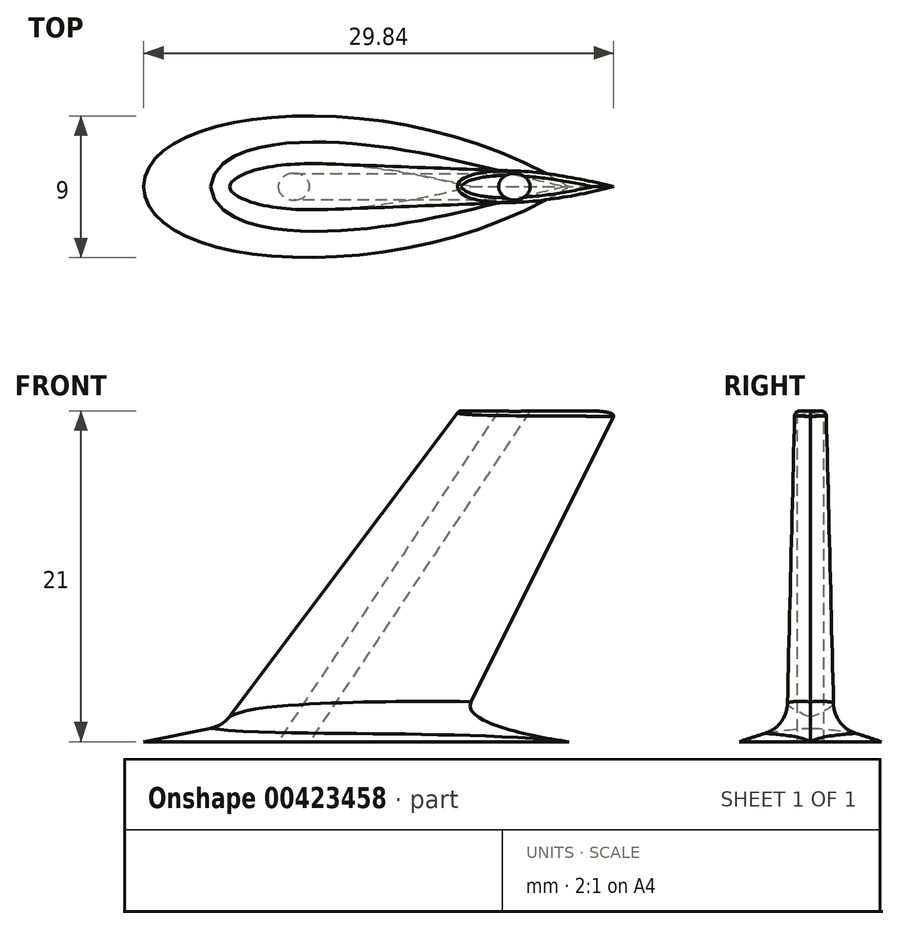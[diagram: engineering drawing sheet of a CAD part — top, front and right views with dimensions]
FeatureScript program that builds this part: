
annotation { "Feature Type Name" : "Feature", "Feature Type Description" : "" }
export const myFeature = defineFeature(function(context is Context, id is Id, definition is map)
    precondition{}
    {
        {
            var Q0;
            Q0=qCreatedBy(makeId("Top.planeOp"),FACE);
            var sketch = newSketch(context, id + "F0", { "sketchPlane" : qUnion([Q0])});
            skLineSegment(sketch, "E0", {"start": v(-14.02, 0) * mm, "end": v(17.18, 0) * mm, "construction": true});
            skLineSegment(sketch, "E1", {"start": v(-5, 5.24) * mm, "end": v(-5, -5.85) * mm, "construction": true});
            skLineSegment(sketch, "E2", {"start": v(10, 3.87) * mm, "end": v(10, -6.39) * mm, "construction": true});
            skFitSpline(sketch, "E3", {"points": [v(-5, 0) * mm, v(10, 0) * mm], "startDerivative": vector(0, 3.68) * mm, "endDerivative": vector(32.22, -7.95) * mm});
            skLineSegment(sketch, "E4", {"start": v(-7.07, 1.5) * mm, "end": v(10, 1.5) * mm, "construction": true});
            skFitSpline(sketch, "E5.MirrorCS", {"points": [v(-5, 0) * mm, v(10, 0) * mm], "startDerivative": vector(0, -3.68) * mm, "endDerivative": vector(32.22, 7.95) * mm});
            skSolve(sketch);
        }
        {
            var Q0;
            Q0=qCreatedBy(makeId("Top.planeOp"),FACE);
            cPlane(context, id + "F1", {"entities" : qUnion([Q0]), "cplaneType" : CPlaneType.OFFSET, "offset" : 20 * mm, "width" : 150 * mm, "height" : 150 * mm});
        }
        {
            var Q0;
            Q0=qCreatedBy(id+"F1.planeOp",FACE);
            var sketch = newSketch(context, id + "F2", { "sketchPlane" : qUnion([Q0])});
            skLineSegment(sketch, "E6.0", {"start": v(-14.02, 0) * mm, "end": v(17.18, 0) * mm, "construction": true});
            skLineSegment(sketch, "E7", {"start": v(20, 4.64) * mm, "end": v(20, -5.96) * mm, "construction": true});
            skLineSegment(sketch, "E8", {"start": v(10, 6.56) * mm, "end": v(10, -5.72) * mm, "construction": true});
            skLineSegment(sketch, "E9", {"start": v(-6.91, 1) * mm, "end": v(15.44, 1) * mm, "construction": true});
            skLineSegment(sketch, "E10", {"start": v(13.33, 5.56) * mm, "end": v(13.33, -4.6) * mm, "construction": true});
            skFitSpline(sketch, "E11", {"points": [v(10, 0) * mm, v(20, 0) * mm], "startDerivative": vector(0, 1.98) * mm, "endDerivative": vector(22.73, -5.62) * mm});
            skFitSpline(sketch, "E12.MirrorCS", {"points": [v(10, 0) * mm, v(20, 0) * mm], "startDerivative": vector(0, -1.98) * mm, "endDerivative": vector(22.73, 5.62) * mm});
            skSolve(sketch);
        }
        {
            var Q0;
            Q0 = qSketchRegion(id + "F0", true);
            var Q1;
            Q1 = qSketchRegion(id + "F2", true);
            loft(context, id + "F3", {"sheetProfilesArray" : [{ "sheetProfileEntities" : qUnion([Q0]) }, { "sheetProfileEntities" : qUnion([Q1]) }]});
        }
        {
            var Q0;
            Q0=makeQuery(id+"F3.opLoft","CAP_FACE",FACE,{"disambiguationData":[OSD([makeQuery(id+"F2.imprint","IMPRINT",FACE,{"disambiguationData":[TD([[makeQuery(id+"F2.imprint","IMPRINT",EDGE,{"derivedFrom":sQuery(id+"F2.wireOp",EDGE,"E11")}),-1.0]])]})])],"isStart":true});
            var sketch = newSketch(context, id + "F4", { "sketchPlane" : qUnion([Q0])});
            skFitSpline(sketch, "E13.0", {"points": [v(10, 0) * mm, v(10, -0.66) * mm, v(12.42, -1.87) * mm, v(20, 0) * mm]});
            skLineSegment(sketch, "E14", {"start": v(10, 0) * mm, "end": v(20, 0) * mm});
            skLineSegment(sketch, "E15.0", {"start": v(13.33, 5.56) * mm, "end": v(13.33, -4.6) * mm, "construction": true});
            skPoint(sketch, "E16", {"position": v(13.33, -1) * mm});
            skSolve(sketch);
        }
        {
            var Q0;
            Q0=sQuery(id+"F2.wireOp",EDGE,"E10");
            cPlane(context, id + "F5", {"entities" : qUnion([Q0]), "cplaneType" : CPlaneType.LINE_ANGLE, "offset" : 25 * mm, "angle" : 90 * degree, "width" : 150 * mm, "height" : 150 * mm});
        }
        {
            var Q0;
            Q0=qCreatedBy(makeId("Front.planeOp"),FACE);
            var sketch = newSketch(context, id + "F6", { "sketchPlane" : qUnion([Q0])});
            skFitSpline(sketch, "E17.0", {"points": [v(10, 20) * mm, v(13.33, 20) * mm, v(16.67, 20) * mm, v(20, 20) * mm]});
            skFitSpline(sketch, "E18", {"points": [v(10, 20) * mm, v(20, 20) * mm], "startDerivative": vector(3.78, 4.68) * mm, "endDerivative": vector(13.44, -3.26) * mm});
            skFitSpline(sketch, "E19", {"points": [v(-5, 0) * mm, v(0, 6.67) * mm, v(5, 13.33) * mm, v(10, 20) * mm], "construction": true});
            skFitSpline(sketch, "E20.0", {"points": [v(10, 21) * mm, v(13.33, 21) * mm, v(16.67, 21) * mm, v(20, 21) * mm], "construction": true});
            skPoint(sketch, "E21", {"position": v(13.33, 21) * mm});
            skLineSegment(sketch, "E22", {"start": v(13.33, 21.42) * mm, "end": v(13.33, 20.86) * mm, "construction": true});
            skSolve(sketch);
        }
        {
            var Q0;
            Q0=makeQuery(id+"F4.imprint","IMPRINT",FACE,{"disambiguationData":[TD([[makeQuery(id+"F4.imprint","IMPRINT",EDGE,{"derivedFrom":sQuery(id+"F4.wireOp",EDGE,"E14")}),1.0]])]});
            var sketch = newSketch(context, id + "F7", { "sketchPlane" : qUnion([Q0])});
            skLineSegment(sketch, "E23.0", {"start": v(13.33, 5.56) * mm, "end": v(13.33, -4.6) * mm, "construction": true});
            skLineSegment(sketch, "E24.0", {"start": v(-14.02, 0) * mm, "end": v(17.18, 0) * mm, "construction": true});
            skEllipse(sketch, "E25", {"center": v(13.33, 0) * mm, "majorRadius": 0.8 * mm, "minorRadius": 0.6 * mm, "majorAxis": v(1, 0)});
            skSolve(sketch);
        }
        {
            var Q0;
            Q0=qCreatedBy(makeId("Front.planeOp"),FACE);
            var sketch = newSketch(context, id + "F8", { "sketchPlane" : qUnion([Q0])});
            skLineSegment(sketch, "E26.0", {"start": v(0.8, 0) * mm, "end": v(-0.8, 0) * mm, "construction": true});
            skLineSegment(sketch, "E27.0", {"start": v(12.53, 20) * mm, "end": v(14.13, 20) * mm, "construction": true});
            skLineSegment(sketch, "E28", {"start": v(-2.77, -2.96) * mm, "end": v(12.53, 20) * mm});
            skLineSegment(sketch, "E29", {"start": v(0.8, 0) * mm, "end": v(14.13, 20) * mm, "construction": true});
            skSolve(sketch);
        }
        {
            var Q0;
            Q0=qCreatedBy(makeId("Top.planeOp"),FACE);
            cPlane(context, id + "F9", {"entities" : qUnion([Q0]), "cplaneType" : CPlaneType.OFFSET, "offset" : 1 * mm, "oppositeDirection" : true, "width" : 150 * mm, "height" : 150 * mm});
        }
        {
            var Q0;
            Q0=qCreatedBy(id+"F9.planeOp",FACE);
            var sketch = newSketch(context, id + "F10", { "sketchPlane" : qUnion([Q0])});
            skLineSegment(sketch, "E30", {"start": v(-10.67, 0) * mm, "end": v(24.23, 0) * mm, "construction": true});
            skLineSegment(sketch, "E31", {"start": v(0, 7.05) * mm, "end": v(0, -8.28) * mm, "construction": true});
            skLineSegment(sketch, "E32", {"start": v(-10, -6.39) * mm, "end": v(-10, 7.63) * mm, "construction": true});
            skLineSegment(sketch, "E33", {"start": v(17, -8) * mm, "end": v(17, 7.72) * mm, "construction": true});
            skLineSegment(sketch, "E34", {"start": v(-14.02, -4.5) * mm, "end": v(25.98, -4.5) * mm, "construction": true});
            skFitSpline(sketch, "E35", {"points": [v(-10, 0) * mm, v(17, 0) * mm], "startDerivative": vector(0, -15.76) * mm, "endDerivative": vector(32.24, 20.1) * mm});
            skFitSpline(sketch, "E36.MirrorCS", {"points": [v(-10, 0) * mm, v(17, 0) * mm], "startDerivative": vector(0, 15.76) * mm, "endDerivative": vector(32.24, -20.1) * mm});
            skSolve(sketch);
        }
        {
            var Q1;
            Q1 = qSketchRegion(id + "F10", true);
            var Q2;
            Q2 = qSketchRegion(id + "F0", true);
            loft(context, id + "F11", {"operationType" : NewBodyOperationType.ADD, "sheetProfilesArray" : [{ "sheetProfileEntities" : qUnion([Q1]) }, { "sheetProfileEntities" : qUnion([Q2]) }]});
        }
        {
            var Q0;
            {var subQ0=sQuery(id+"F0.wireOp",EDGE,"E3");var subQ1=makeQuery(id+"F0.imprint","IMPRINT",EDGE,{"derivedFrom":subQ0});var subQ2=sQuery(id+"F0.wireOp",EDGE,"E5.MirrorCS");var subQ3=makeQuery(id+"F0.imprint","INTERSECT",VERTEX,{"disambiguationData":[OD(1.0)],"derivedFrom":[subQ0,subQ2]});var subQ4=makeQuery(id+"F0.imprint","INTERSECT",VERTEX,{"disambiguationData":[OD(0.0)],"derivedFrom":[subQ0,subQ2]});Q0=makeQuery(id+"F11.boolean.opBoolean","MERGE",EDGE,{"derivedFrom":[makeQuery(id+"F3.opLoft","MID_CAP_EDGE",EDGE,{"disambiguationData":[OSD([subQ0,subQ2]),TDD([subQ4,subQ3,subQ1])],"capPos":0.0}),makeQuery(id+"F11.opLoft","MID_CAP_EDGE",EDGE,{"disambiguationData":[OSD([subQ0,subQ2]),TDD([subQ4,subQ3,subQ1])],"capPos":1.0})]});}
            var Q1;
            {var subQ0=sQuery(id+"F0.wireOp",EDGE,"E5.MirrorCS");var subQ1=makeQuery(id+"F0.imprint","IMPRINT",EDGE,{"derivedFrom":subQ0});var subQ2=sQuery(id+"F0.wireOp",EDGE,"E3");var subQ3=makeQuery(id+"F0.imprint","INTERSECT",VERTEX,{"disambiguationData":[OD(1.0)],"derivedFrom":[subQ2,subQ0]});var subQ4=makeQuery(id+"F0.imprint","INTERSECT",VERTEX,{"disambiguationData":[OD(0.0)],"derivedFrom":[subQ2,subQ0]});Q1=makeQuery(id+"F11.boolean.opBoolean","MERGE",EDGE,{"derivedFrom":[makeQuery(id+"F3.opLoft","MID_CAP_EDGE",EDGE,{"disambiguationData":[OSD([subQ2,subQ0]),TDD([subQ4,subQ3,subQ1])],"capPos":0.0}),makeQuery(id+"F11.opLoft","MID_CAP_EDGE",EDGE,{"disambiguationData":[OSD([subQ2,subQ0]),TDD([subQ4,subQ3,subQ1])],"capPos":1.0})]});}
            fillet(context, id + "F12", {"entities" : qUnion([Q0, Q1]), "radius" : 2 * mm, "tangentPropagation" : true, "allowEdgeOverflow" : false});
        }
        {
            var Q0;
            Q0=makeQuery(id+"F3.opLoft","CAP_FACE",FACE,{"disambiguationData":[OSD([makeQuery(id+"F2.imprint","IMPRINT",FACE,{"disambiguationData":[TD([[makeQuery(id+"F2.imprint","IMPRINT",EDGE,{"derivedFrom":sQuery(id+"F2.wireOp",EDGE,"E11")}),-1.0]])]})])],"isStart":true});
            fillet(context, id + "F13", {"entities" : qUnion([Q0]), "radius" : 0.3 * mm, "allowEdgeOverflow" : false});
        }
        {
            var Q0;
            Q0=makeQuery(id+"F11.opLoft","CAP_FACE",FACE,{"disambiguationData":[OSD([makeQuery(id+"F10.imprint","IMPRINT",FACE,{"disambiguationData":[TD([[makeQuery(id+"F10.imprint","IMPRINT",EDGE,{"derivedFrom":sQuery(id+"F10.wireOp",EDGE,"E35")}),1.0]])]})])],"isStart":true});
            var sketch = newSketch(context, id + "F14", { "sketchPlane" : qUnion([Q0])});
            skLineSegment(sketch, "E37.0", {"start": v(-2.77, 0) * mm, "end": v(12.53, 0) * mm, "construction": true});
            skPoint(sketch, "E38", {"position": v(-1.47, 0) * mm});
            skEllipse(sketch, "E39", {"center": v(-0.47, 0) * mm, "majorRadius": 1 * mm, "minorRadius": 0.85 * mm, "majorAxis": v(-1, 0)});
            skSolve(sketch);
        }
        {
            var Q0;
            Q0 = qSketchRegion(id + "F7", true);
            var Q1;
            Q1 = qSketchRegion(id + "F14", true);
            var Q2;
            Q2=sQuery(id+"F8.wireOp",EDGE,"E28");
            sweep(context, id + "F15", {"operationType" : NewBodyOperationType.REMOVE, "profiles" : qUnion([Q0, Q1]), "path" : qUnion([Q2])});
        }
    });
